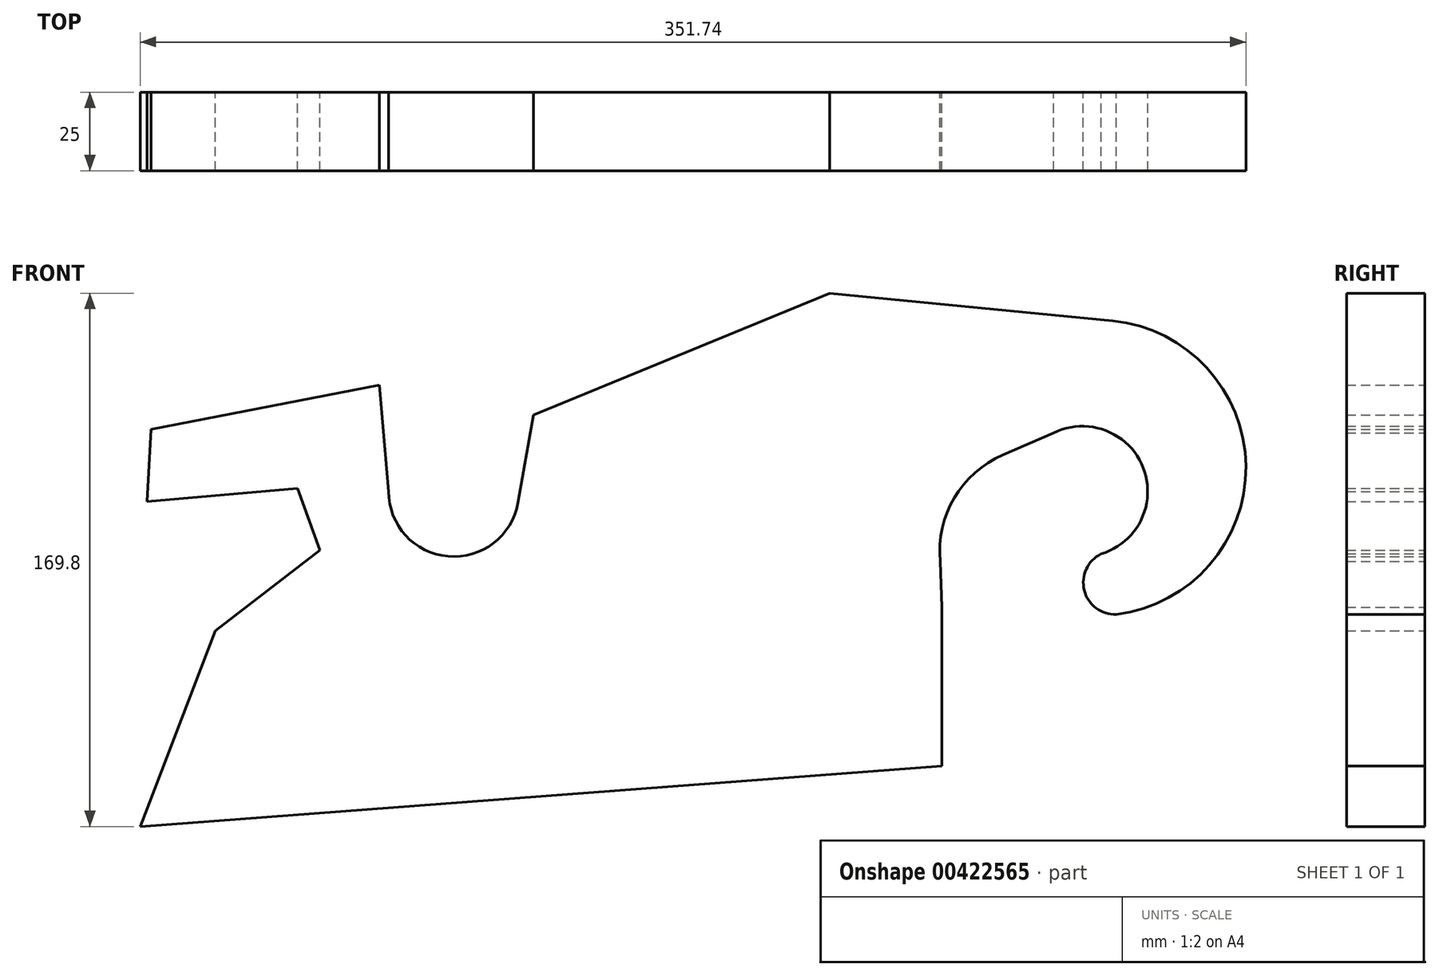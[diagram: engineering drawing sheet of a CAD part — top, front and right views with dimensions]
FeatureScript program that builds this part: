
annotation { "Feature Type Name" : "Feature", "Feature Type Description" : "" }
export const myFeature = defineFeature(function(context is Context, id is Id, definition is map)
    precondition{}
    {
        {
            var Q0;
            Q0=qCreatedBy(makeId("Front.planeOp"),FACE);
            var sketch = newSketch(context, id + "F0", { "sketchPlane" : qUnion([Q0])});
            skArc(sketch, "E0", {"start": v(-20.75, 0) * mm, "mid": v(-1.8, -20.67) * mm, "end": v(20.44, -3.57) * mm});
            skArc(sketch, "E1", {"start": v(202, -20.65) * mm, "mid": v(219.96, 5.67) * mm, "end": v(190.84, 18.62) * mm});
            skLineSegment(sketch, "E2", {"start": v(-223.61, 0) * mm, "end": v(377.72, 0) * mm});
            skLineSegment(sketch, "E3", {"start": v(-20.75, 0) * mm, "end": v(-23.71, 33.87) * mm});
            skLineSegment(sketch, "E4", {"start": v(25.31, 24.3) * mm, "end": v(119.63, 63.12) * mm});
            skArc(sketch, "E5", {"start": v(202, -39.4) * mm, "mid": v(251.85, 3.7) * mm, "end": v(209.6, 54.27) * mm});
            skLineSegment(sketch, "E6", {"start": v(119.63, 63.12) * mm, "end": v(209.6, 54.27) * mm});
            skLineSegment(sketch, "E7", {"start": v(200, 0) * mm, "end": v(202, 0) * mm});
            skLineSegment(sketch, "E8", {"start": v(202, -20.65) * mm, "end": v(202, -39.4) * mm});
            skLineSegment(sketch, "E9", {"start": v(-23.71, 33.87) * mm, "end": v(-96.35, 19.75) * mm});
            skLineSegment(sketch, "E10", {"start": v(-96.35, 19.75) * mm, "end": v(-97.56, -3.22) * mm});
            skLineSegment(sketch, "E11", {"start": v(-97.56, -3.22) * mm, "end": v(-49.74, 0.97) * mm});
            skLineSegment(sketch, "E12", {"start": v(-49.74, 0.97) * mm, "end": v(-42.56, -18.77) * mm});
            skLineSegment(sketch, "E13", {"start": v(-42.56, -18.77) * mm, "end": v(-75.88, -44.34) * mm});
            skLineSegment(sketch, "E14", {"start": v(200, 0) * mm, "end": v(154, 0) * mm});
            skLineSegment(sketch, "E15", {"start": v(154.63, -18) * mm, "end": v(155.29, -36.92) * mm});
            skArc(sketch, "E16", {"start": v(174.72, 11.63) * mm, "mid": v(159.21, -2.1) * mm, "end": v(154.78, -22.33) * mm});
            skLineSegment(sketch, "E17", {"start": v(192.68, 19.41) * mm, "end": v(174.72, 11.63) * mm});
            skLineSegment(sketch, "E18", {"start": v(-75.88, -44.34) * mm, "end": v(-99.74, -106.68) * mm});
            skLineSegment(sketch, "E19", {"start": v(-99.74, -106.68) * mm, "end": v(155.29, -87.45) * mm});
            skLineSegment(sketch, "E20", {"start": v(155.29, -87.45) * mm, "end": v(155.29, -36.92) * mm});
            skLineSegment(sketch, "E21", {"start": v(25.31, 24.3) * mm, "end": v(20.44, -3.57) * mm});
            skArc(sketch, "E22", {"start": v(205.91, -19.9) * mm, "mid": v(200.6, -31.48) * mm, "end": v(210.8, -39.14) * mm});
            skSolve(sketch);
        }
        {
            var Q0;
            {var subQ0=sQuery(id+"F0.wireOp",EDGE,"E22");var subQ8=sQuery(id+"F0.wireOp",EDGE,"E1");var subQ10=makeQuery(id+"F0.imprint","INTERSECT",VERTEX,{"derivedFrom":[subQ8,subQ0]});Q0=makeQuery(id+"F0.imprint","IMPRINT",FACE,{"disambiguationData":[TD([[makeQuery(id+"F0.imprint","IMPRINT",EDGE,{"disambiguationData":[TD([[subQ10,-1.0]])],"derivedFrom":subQ8}),-1.0]])]});}
            var Q1;
            {var subQ0=sQuery(id+"F0.wireOp",EDGE,"E22");var subQ1=sQuery(id+"F0.wireOp",EDGE,"E8");var subQ2=makeQuery(id+"F0.imprint","INTERSECT",VERTEX,{"disambiguationData":[OD(0.0)],"derivedFrom":[subQ1,subQ0]});Q1=makeQuery(id+"F0.imprint","IMPRINT",FACE,{"disambiguationData":[TD([[makeQuery(id+"F0.imprint","IMPRINT",EDGE,{"disambiguationData":[TD([[subQ2,-1.0]])],"derivedFrom":subQ1}),-1.0]])]});}
            var Q2;
            {var subQ12=sQuery(id+"F0.wireOp",EDGE,"E4");Q2=makeQuery(id+"F0.imprint","IMPRINT",FACE,{"disambiguationData":[TD([[makeQuery(id+"F0.imprint","IMPRINT",EDGE,{"derivedFrom":subQ12}),-1.0]])]});}
            var Q3;
            {var subQ7=sQuery(id+"F0.wireOp",EDGE,"E0");Q3=makeQuery(id+"F0.imprint","IMPRINT",FACE,{"disambiguationData":[TD([[makeQuery(id+"F0.imprint","IMPRINT",EDGE,{"derivedFrom":subQ7}),-1.0]])]});}
            var Q4;
            {var subQ1=sQuery(id+"F0.wireOp",EDGE,"E3");Q4=makeQuery(id+"F0.imprint","IMPRINT",FACE,{"disambiguationData":[TD([[makeQuery(id+"F0.imprint","IMPRINT",EDGE,{"derivedFrom":subQ1}),1.0]])]});}
            var Q5;
            {var subQ0=sQuery(id+"F0.wireOp",EDGE,"E10");var subQ1=sQuery(id+"F0.wireOp",EDGE,"E2");var subQ2=makeQuery(id+"F0.imprint","INTERSECT",VERTEX,{"derivedFrom":[subQ1,subQ0]});Q5=makeQuery(id+"F0.imprint","IMPRINT",FACE,{"disambiguationData":[TD([[makeQuery(id+"F0.imprint","IMPRINT",EDGE,{"disambiguationData":[TD([[subQ2,-1.0]])],"derivedFrom":subQ1}),-1.0]])]});}
            extrude(context, id + "F1", {"entities" : qUnion([Q0, Q1, Q2, Q3, Q4, Q5]), "depth" : 25 * mm, "offsetDistance" : 25 * mm});
        }
    });
